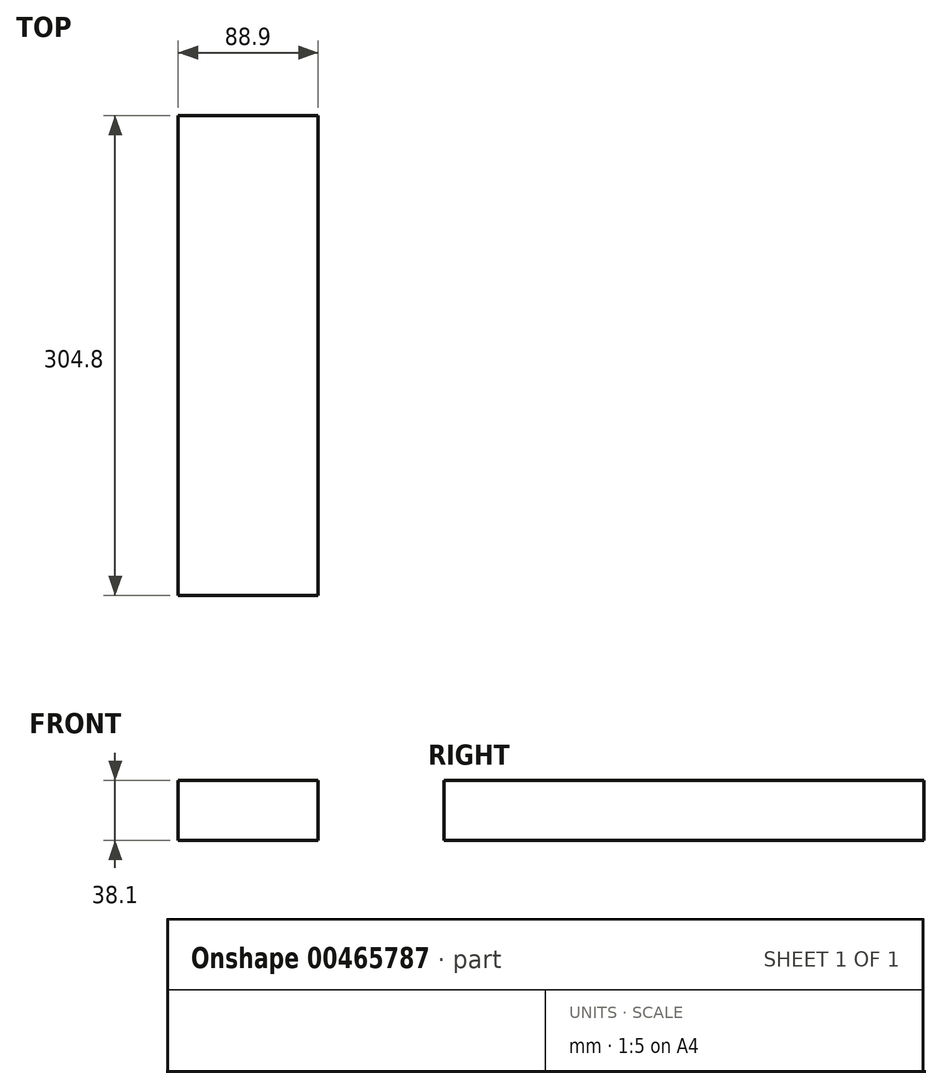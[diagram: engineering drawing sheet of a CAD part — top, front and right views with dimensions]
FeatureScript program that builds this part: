
annotation { "Feature Type Name" : "Feature", "Feature Type Description" : "" }
export const myFeature = defineFeature(function(context is Context, id is Id, definition is map)
    precondition{}
    {
        {
            var Q0;
            Q0=qCreatedBy(makeId("Front.planeOp"),FACE);
            var sketch = newSketch(context, id + "F0", { "sketchPlane" : qUnion([Q0])});
            skLineSegment(sketch, "E0.bottom", {"start": v(44.45, 19.05) * mm, "end": v(-44.45, 19.05) * mm});
            skLineSegment(sketch, "E0.top", {"start": v(44.45, -19.05) * mm, "end": v(-44.45, -19.05) * mm});
            skLineSegment(sketch, "E0.left", {"start": v(44.45, 19.05) * mm, "end": v(44.45, -19.05) * mm});
            skLineSegment(sketch, "E0.right", {"start": v(-44.45, 19.05) * mm, "end": v(-44.45, -19.05) * mm});
            skPoint(sketch, "E0.middle", {"position": v(0, 0) * mm});
            skSolve(sketch);
        }
        {
            var Q0;
            Q0=makeQuery(id+"F0.imprint","IMPRINT",FACE,{"disambiguationData":[TD([[makeQuery(id+"F0.imprint","IMPRINT",EDGE,{"derivedFrom":sQuery(id+"F0.wireOp",EDGE,"E0.bottom")}),1.0]])]});
            extrude(context, id + "F1", {"entities" : qUnion([Q0]), "endBound" : BoundingType.SYMMETRIC, "depth" : 304.8 * mm});
        }
    });
